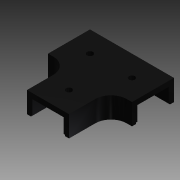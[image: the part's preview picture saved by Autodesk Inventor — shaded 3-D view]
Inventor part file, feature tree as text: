
AUTODESK INVENTOR PART (.ipt)
format: ipt  version: 2015 (Build 190159000, 159)  size: 174,080 bytes
history: native  units: in
note: dims shown in document units (in); Inventor stores cm internally (conversion verified against a paired STEP export)
features: extrude x6, sketch x6, other x3, split x1, fillet x1
ambient origin geometry x8: Origin, YZ Plane, XZ Plane, XY Plane, X Axis, Y Axis, Z Axis, Center Point
bodies: Solid1 (feature_tree)
feature tree (17):
  extrude  "Extrusion1"  Depth=1.0in
  extrude  "Extrusion2"  Depth=0.5in TaperAngle=0.0deg
  extrude  "Extrusion3"  Depth=0.75in
  extrude  "Extrusion4"  Depth=1.75in TaperAngle=0.0deg
  extrude  "Extrusion5"  Depth=0.75in
  split  "Split1"
  other  "Lip1"
  other  "Lip2"
  other  "Lip3"
  extrude  "Extrusion6"  Depth=0.375in
  fillet  "Fillet1"  Radius=1.0in
  sketch  "Sketch1"  dims[d0=1.0in d1=1.0in]
  sketch  "Sketch2"  dims[d2=2.0in d3=0.0in d4=0.5in d5=0.0in]
  sketch  "Sketch4"  dims[d6=0.5in d7=0.0in d8=0.75in]
  sketch  "Sketch5"  dims[d9=0.75in d10=1.75in d11=0.0in]
  sketch  "Sketch6"  dims[d12=0.75in d13=0.75in]
  sketch  "Sketch7"  dims[d14=1.75in d15=0.0in d16=0.03in d17=0.03in d18=0.0in d19=0.0in d20=0.0in d21=0.0in d22=0.03in d23=0.03in d24=0.0in d25=0.0in d26=0.0in d27=0.0in d28=0.03in d29=0.03in d30=0.0in d31=0.0in d32=0.0in d33=0.0in d34=0.141in d35=1.0in d36=0.0in d37=0.375in]
